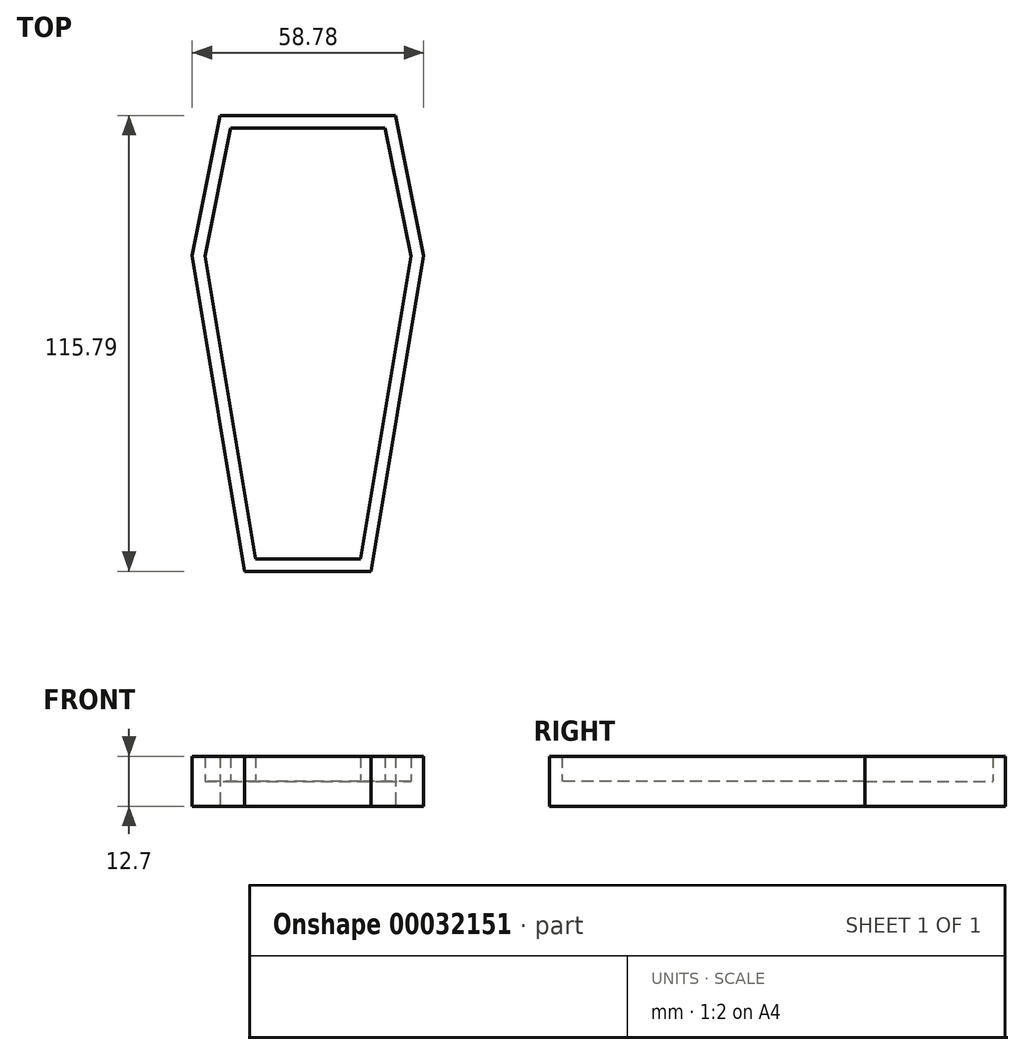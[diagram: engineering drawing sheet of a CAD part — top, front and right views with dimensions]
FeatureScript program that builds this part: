
annotation { "Feature Type Name" : "Feature", "Feature Type Description" : "" }
export const myFeature = defineFeature(function(context is Context, id is Id, definition is map)
    precondition{}
    {
        {
            var Q0;
            Q0=qCreatedBy(makeId("Top.planeOp"),FACE);
            var sketch = newSketch(context, id + "F0", { "sketchPlane" : qUnion([Q0])});
            skLineSegment(sketch, "E0", {"start": v(-19.05, 31.75) * mm, "end": v(19.05, 31.75) * mm});
            skLineSegment(sketch, "E1", {"start": v(19.05, 31.75) * mm, "end": v(25.4, 0) * mm});
            skLineSegment(sketch, "E2", {"start": v(25.4, 0) * mm, "end": v(12.7, -76.2) * mm});
            skLineSegment(sketch, "E3", {"start": v(12.7, -76.2) * mm, "end": v(-12.7, -76.2) * mm});
            skLineSegment(sketch, "E4", {"start": v(-12.7, -76.2) * mm, "end": v(-25.4, 0) * mm});
            skLineSegment(sketch, "E5", {"start": v(-25.4, 0) * mm, "end": v(-19.05, 31.75) * mm});
            skLineSegment(sketch, "E6", {"start": v(0, 0) * mm, "end": v(0, 31.75) * mm});
            skLineSegment(sketch, "E7.0", {"start": v(19.66, 32.5) * mm, "end": v(26.16, 0.01) * mm});
            skLineSegment(sketch, "E7.1", {"start": v(-19.66, 32.5) * mm, "end": v(19.66, 32.5) * mm});
            skLineSegment(sketch, "E7.2", {"start": v(-26.16, 0.01) * mm, "end": v(-19.66, 32.5) * mm});
            skLineSegment(sketch, "E7.3", {"start": v(-13.33, -76.95) * mm, "end": v(-26.16, 0.01) * mm});
            skLineSegment(sketch, "E7.4", {"start": v(13.33, -76.95) * mm, "end": v(-13.33, -76.95) * mm});
            skLineSegment(sketch, "E7.5", {"start": v(26.16, 0.01) * mm, "end": v(13.33, -76.95) * mm});
            skLineSegment(sketch, "E8.0", {"start": v(-29.39, 0.06) * mm, "end": v(-22.27, 35.67) * mm});
            skLineSegment(sketch, "E8.1", {"start": v(-16.02, -80.12) * mm, "end": v(-29.39, 0.06) * mm});
            skLineSegment(sketch, "E8.2", {"start": v(16.02, -80.12) * mm, "end": v(-16.02, -80.12) * mm});
            skLineSegment(sketch, "E8.3", {"start": v(29.39, 0.06) * mm, "end": v(16.02, -80.12) * mm});
            skLineSegment(sketch, "E8.4", {"start": v(22.27, 35.67) * mm, "end": v(29.39, 0.06) * mm});
            skLineSegment(sketch, "E8.5", {"start": v(-22.27, 35.67) * mm, "end": v(22.27, 35.67) * mm});
            skSolve(sketch);
        }
        {
            var Q0;
            Q0 = qSketchRegion(id + "F0", true);
            var Q1;
            {var subQ1=sQuery(id+"F0.wireOp",EDGE,"E1");Q1=makeQuery(id+"F0.imprint","IMPRINT",FACE,{"disambiguationData":[TD([[makeQuery(id+"F0.imprint","IMPRINT",EDGE,{"derivedFrom":subQ1}),-1.0]])]});}
            var Q2;
            {var subQ1=sQuery(id+"F0.wireOp",EDGE,"E1");Q2=makeQuery(id+"F0.imprint","IMPRINT",FACE,{"disambiguationData":[TD([[makeQuery(id+"F0.imprint","IMPRINT",EDGE,{"derivedFrom":subQ1}),1.0]])]});}
            extrude(context, id + "F1", {"entities" : qUnion([Q0, Q1, Q2]), "depth" : 6.35 * mm});
        }
        {
            var Q0;
            Q0=makeQuery(id+"F1.opExtrude","CAP_FACE",FACE,{"disambiguationData":[OSD([sQuery(id+"F0.wireOp",EDGE,"E8.0"),sQuery(id+"F0.wireOp",EDGE,"E8.1"),sQuery(id+"F0.wireOp",EDGE,"E8.2"),sQuery(id+"F0.wireOp",EDGE,"E8.3"),sQuery(id+"F0.wireOp",EDGE,"E8.4"),sQuery(id+"F0.wireOp",EDGE,"E8.5")])],"isStart":false});
            var sketch = newSketch(context, id + "F2", { "sketchPlane" : qUnion([Q0])});
            skLineSegment(sketch, "E9.0", {"start": v(16.02, -80.12) * mm, "end": v(-16.02, -80.12) * mm});
            skLineSegment(sketch, "E9.1", {"start": v(-16.02, -80.12) * mm, "end": v(-29.39, 0.06) * mm});
            skLineSegment(sketch, "E9.2", {"start": v(29.39, 0.06) * mm, "end": v(16.02, -80.12) * mm});
            skLineSegment(sketch, "E9.3", {"start": v(-29.39, 0.06) * mm, "end": v(-22.27, 35.67) * mm});
            skLineSegment(sketch, "E9.4", {"start": v(-22.27, 35.67) * mm, "end": v(22.27, 35.67) * mm});
            skLineSegment(sketch, "E9.5", {"start": v(22.27, 35.67) * mm, "end": v(29.39, 0.06) * mm});
            skLineSegment(sketch, "E10.0", {"start": v(13.33, -76.95) * mm, "end": v(-13.33, -76.95) * mm});
            skLineSegment(sketch, "E10.1", {"start": v(26.16, 0.01) * mm, "end": v(13.33, -76.95) * mm});
            skLineSegment(sketch, "E10.2", {"start": v(19.66, 32.5) * mm, "end": v(26.16, 0.01) * mm});
            skLineSegment(sketch, "E10.3", {"start": v(-19.66, 32.5) * mm, "end": v(19.66, 32.5) * mm});
            skLineSegment(sketch, "E10.4", {"start": v(-26.16, 0.01) * mm, "end": v(-19.66, 32.5) * mm});
            skLineSegment(sketch, "E10.5", {"start": v(-13.33, -76.95) * mm, "end": v(-26.16, 0.01) * mm});
            skSolve(sketch);
        }
        {
            var Q0;
            Q0 = qSketchRegion(id + "F2", true);
            extrude(context, id + "F3", {"entities" : qUnion([Q0]), "operationType" : NewBodyOperationType.ADD, "depth" : 6.35 * mm});
        }
    });
